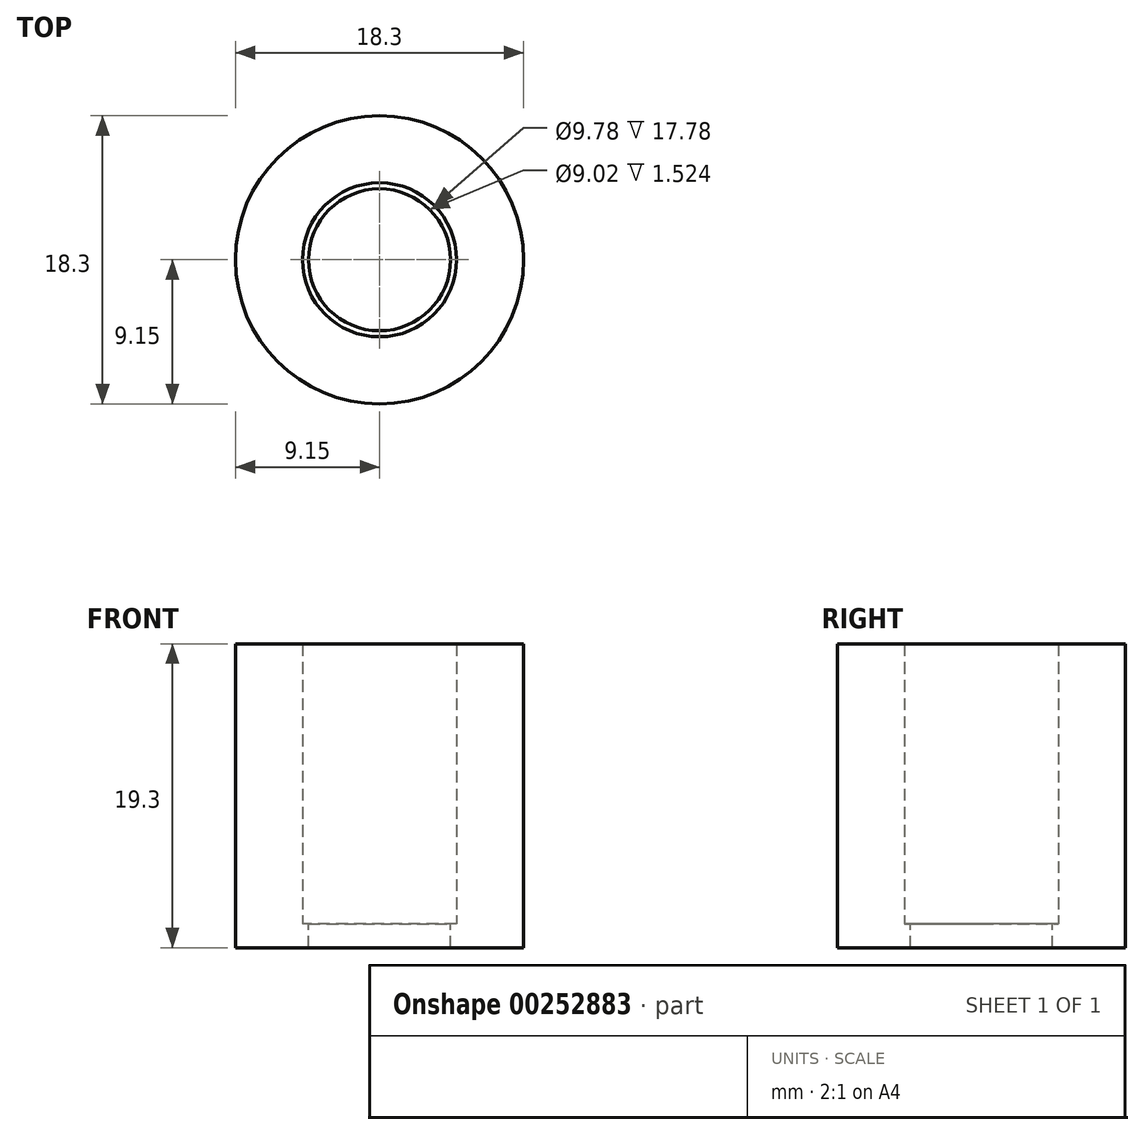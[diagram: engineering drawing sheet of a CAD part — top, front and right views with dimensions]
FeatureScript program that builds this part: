
annotation { "Feature Type Name" : "Feature", "Feature Type Description" : "" }
export const myFeature = defineFeature(function(context is Context, id is Id, definition is map)
    precondition{}
    {
        {
            var Q0;
            Q0=qCreatedBy(makeId("Top.planeOp"),FACE);
            var sketch = newSketch(context, id + "F0", { "sketchPlane" : qUnion([Q0])});
            skCircle(sketch, "E0", {"center": v(0, 0) * mm, "radius": 9.15 * mm});
            skCircle(sketch, "E1", {"center": v(0, 0) * mm, "radius": 4.9 * mm});
            skSolve(sketch);
        }
        {
            var Q0;
            Q0=sQuery(id+"F0.wireOp",EDGE,"E1");
            extrude(context, id + "F1", {"bodyType" : ToolBodyType.SURFACE, "surfaceEntities" : qUnion([Q0]), "depth" : 17.78 * mm});
        }
        {
            var Q0;
            Q0=makeQuery(id+"F0.imprint","IMPRINT",FACE,{"disambiguationData":[TD([[makeQuery(id+"F0.imprint","IMPRINT",EDGE,{"derivedFrom":sQuery(id+"F0.wireOp",EDGE,"E0")}),1.0]])]});
            var Q1;
            Q1=sQuery(id+"F0.wireOp",EDGE,"E0");
            extrude(context, id + "F2", {"entities" : qUnion([Q0]), "surfaceEntities" : qUnion([Q1]), "depth" : 17.78 * mm});
        }
        {
            var Q0;
            Q0=makeQuery(id+"F2.opExtrude","CAP_FACE",FACE,{"disambiguationData":[OSD([sQuery(id+"F0.wireOp",EDGE,"E0"),sQuery(id+"F0.wireOp",EDGE,"E1")])],"isStart":true});
            var sketch = newSketch(context, id + "F3", { "sketchPlane" : qUnion([Q0])});
            skCircle(sketch, "E2.0", {"center": v(0, 0) * mm, "radius": 9.15 * mm});
            skCircle(sketch, "E3", {"center": v(0, 0) * mm, "radius": 4.5 * mm});
            skSolve(sketch);
        }
        {
            var Q0;
            Q0 = qSketchRegion(id + "F3", true);
            extrude(context, id + "F4", {"entities" : qUnion([Q0]), "operationType" : NewBodyOperationType.ADD, "depth" : 1.52 * mm});
        }
    });
